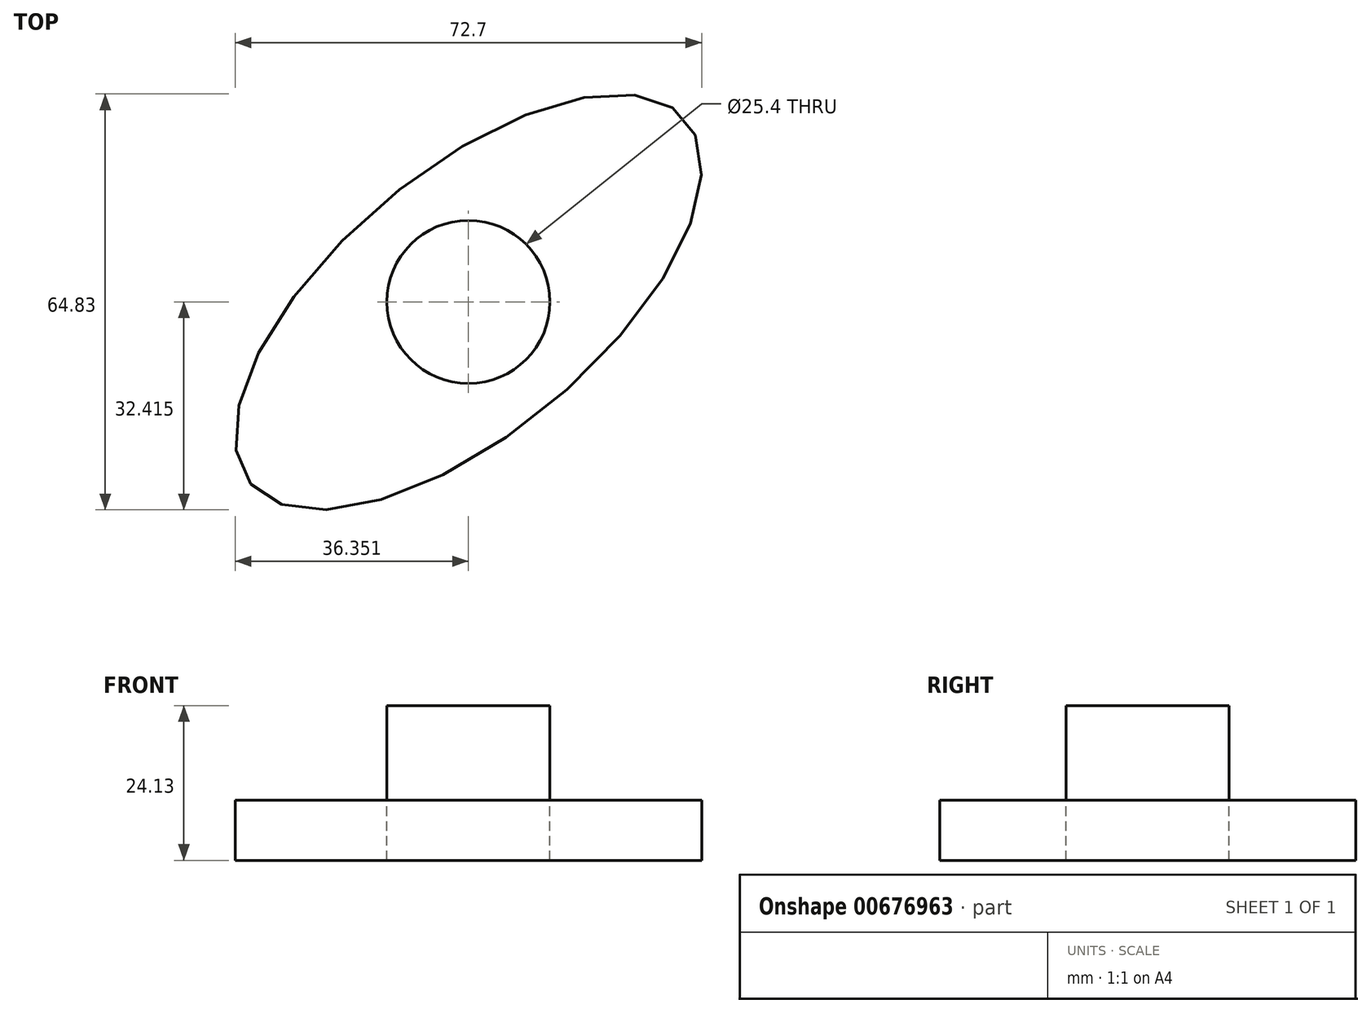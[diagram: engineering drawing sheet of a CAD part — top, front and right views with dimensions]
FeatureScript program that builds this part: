
annotation { "Feature Type Name" : "Feature", "Feature Type Description" : "" }
export const myFeature = defineFeature(function(context is Context, id is Id, definition is map)
    precondition{}
    {
        {
            var Q0;
            Q0=qCreatedBy(makeId("Top.planeOp"),FACE);
            var sketch = newSketch(context, id + "F0", { "sketchPlane" : qUnion([Q0])});
            skEllipse(sketch, "E0", {"center": v(0.27, 0.15) * mm, "majorRadius": 44.23 * mm, "minorRadius": 20.39 * mm, "majorAxis": v(-0.77, -0.64)});
            skCircle(sketch, "E1", {"center": v(0.27, 0.15) * mm, "radius": 12.7 * mm});
            skSolve(sketch);
        }
        {
            var Q0;
            Q0=makeQuery(id+"F0.imprint","IMPRINT",FACE,{"disambiguationData":[TD([[makeQuery(id+"F0.imprint","IMPRINT",EDGE,{"derivedFrom":sQuery(id+"F0.wireOp",EDGE,"E1")}),1.0]])]});
            extrude(context, id + "F1", {"entities" : qUnion([Q0]), "depth" : 14.73 * mm, "offsetDistance" : 25.4 * mm});
        }
        {
            var Q0;
            Q0=sQuery(id+"F0.wireOp",EDGE,"E0");
            extrude(context, id + "F2", {"bodyType" : ToolBodyType.SURFACE, "surfaceEntities" : qUnion([Q0]), "depth" : 25 * mm, "offsetDistance" : 25 * mm});
        }
        {
            var Q0;
            Q0=makeQuery(id+"F0.imprint","IMPRINT",FACE,{"disambiguationData":[TD([[makeQuery(id+"F0.imprint","IMPRINT",EDGE,{"derivedFrom":sQuery(id+"F0.wireOp",EDGE,"E0")}),1.0]])]});
            var Q1;
            Q1=makeQuery(id+"F1.opExtrude","CAP_FACE",FACE,{"disambiguationData":[OSD([sQuery(id+"F0.wireOp",EDGE,"E1")])],"isStart":false});
            extrude(context, id + "F3", {"entities" : qUnion([Q0, Q1]), "operationType" : NewBodyOperationType.ADD, "oppositeDirection" : true, "depth" : 9.4 * mm, "offsetDistance" : 25 * mm});
        }
    });
